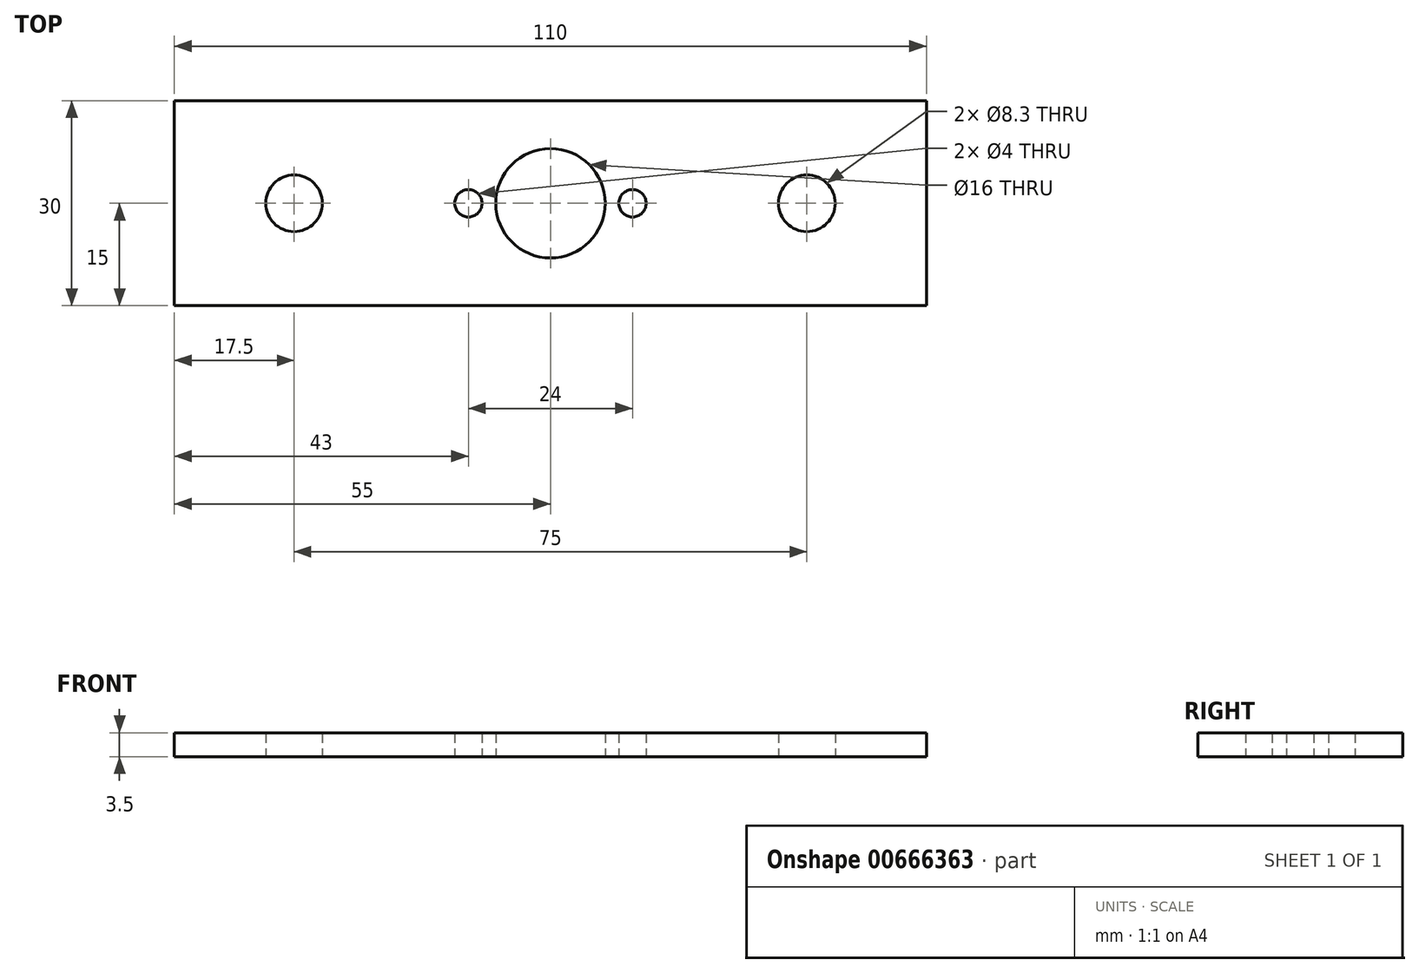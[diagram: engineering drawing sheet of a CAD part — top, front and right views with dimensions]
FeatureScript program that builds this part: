
annotation { "Feature Type Name" : "Feature", "Feature Type Description" : "" }
export const myFeature = defineFeature(function(context is Context, id is Id, definition is map)
    precondition{}
    {
        {
            var Q0;
            Q0=qCreatedBy(makeId("Top.planeOp"),FACE);
            var sketch = newSketch(context, id + "F0", { "sketchPlane" : qUnion([Q0])});
            skLineSegment(sketch, "E0.bottom", {"start": v(-55, 15) * mm, "end": v(55, 15) * mm});
            skLineSegment(sketch, "E0.top", {"start": v(-55, -15) * mm, "end": v(55, -15) * mm});
            skLineSegment(sketch, "E0.left", {"start": v(-55, 15) * mm, "end": v(-55, -15) * mm});
            skLineSegment(sketch, "E0.right", {"start": v(55, 15) * mm, "end": v(55, -15) * mm});
            skPoint(sketch, "E0.middle", {"position": v(0, 0) * mm});
            skCircle(sketch, "E1", {"center": v(-37.5, 0) * mm, "radius": 4.15 * mm});
            skCircle(sketch, "E2.MirrorC", {"center": v(37.5, 0) * mm, "radius": 4.15 * mm});
            skCircle(sketch, "E3", {"center": v(0, 0) * mm, "radius": 8 * mm});
            skCircle(sketch, "E4", {"center": v(-12, 0) * mm, "radius": 2 * mm});
            skCircle(sketch, "E5.MirrorC", {"center": v(12, 0) * mm, "radius": 2 * mm});
            skSolve(sketch);
        }
        {
            var Q0;
            Q0=makeQuery(id+"F0.imprint","IMPRINT",FACE,{"disambiguationData":[TD([[makeQuery(id+"F0.imprint","IMPRINT",EDGE,{"derivedFrom":sQuery(id+"F0.wireOp",EDGE,"E0.bottom")}),-1.0]])]});
            extrude(context, id + "F1", {"entities" : qUnion([Q0]), "depth" : 3.5 * mm, "offsetDistance" : 25.4 * mm});
        }
    });
